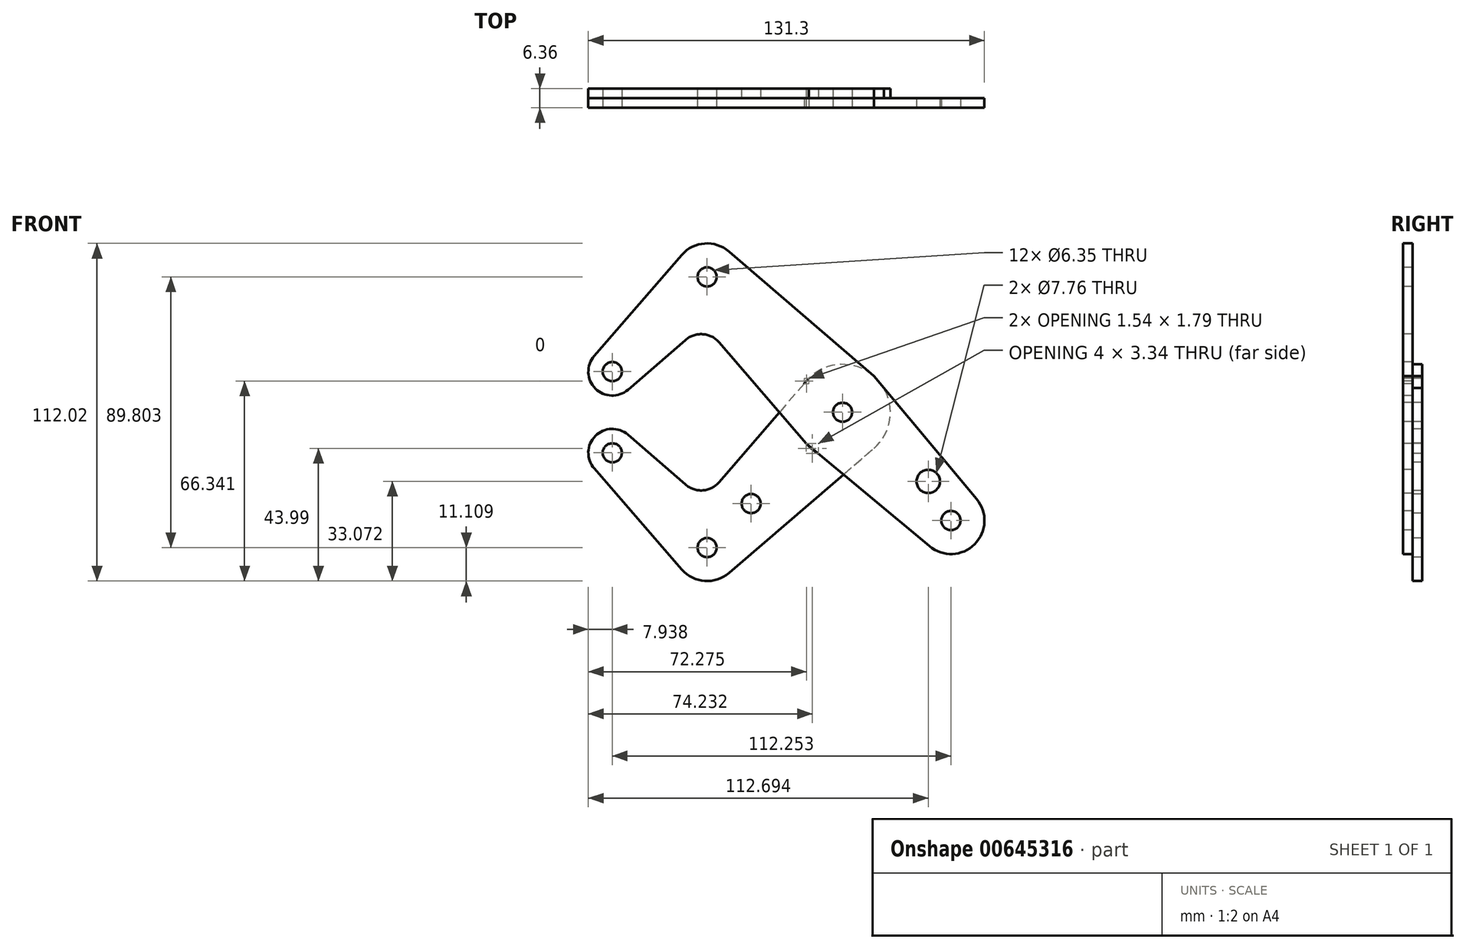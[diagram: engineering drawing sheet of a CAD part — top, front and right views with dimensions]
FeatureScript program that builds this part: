
annotation { "Feature Type Name" : "Feature", "Feature Type Description" : "" }
export const myFeature = defineFeature(function(context is Context, id is Id, definition is map)
    precondition{}
    {
        {
            var Q0;
            Q0=qCreatedBy(makeId("Front.planeOp"),FACE);
            var sketch = newSketch(context, id + "F0", { "sketchPlane" : qUnion([Q0])});
            skLineSegment(sketch, "E0", {"start": v(-76.33, 13.47) * mm, "end": v(-44.9, 44.9) * mm, "construction": true});
            skLineSegment(sketch, "E1", {"start": v(-44.9, 44.9) * mm, "end": v(35.92, -35.92) * mm, "construction": true});
            skCircle(sketch, "E2", {"center": v(-76.33, 13.47) * mm, "radius": 7.94 * mm});
            skCircle(sketch, "E3", {"center": v(-76.33, 13.47) * mm, "radius": 3.18 * mm});
            skCircle(sketch, "E4", {"center": v(-44.9, 44.9) * mm, "radius": 11.11 * mm});
            skCircle(sketch, "E5", {"center": v(-44.9, 44.9) * mm, "radius": 3.18 * mm});
            skCircle(sketch, "E6", {"center": v(0, 0) * mm, "radius": 15.88 * mm});
            skCircle(sketch, "E7", {"center": v(0, 0) * mm, "radius": 3.18 * mm});
            skCircle(sketch, "E8", {"center": v(35.92, -35.92) * mm, "radius": 3.18 * mm});
            skCircle(sketch, "E9", {"center": v(35.92, -35.92) * mm, "radius": 11.11 * mm});
            skCircle(sketch, "E10", {"center": v(0, 0) * mm, "radius": 3.98 * mm});
            skCircle(sketch, "E11", {"center": v(28.42, -22.94) * mm, "radius": 3.88 * mm});
            skLineSegment(sketch, "E12", {"start": v(-82.33, 18.67) * mm, "end": v(-53.3, 52.18) * mm});
            skLineSegment(sketch, "E13", {"start": v(-52.08, 23.98) * mm, "end": v(-71.13, 7.47) * mm});
            skLineSegment(sketch, "E14", {"start": v(-37.66, 53.33) * mm, "end": v(10.35, 12.04) * mm});
            skLineSegment(sketch, "E15", {"start": v(-40.85, 23.15) * mm, "end": v(-12.04, -10.35) * mm});
            skLineSegment(sketch, "E16", {"start": v(10.35, 12.04) * mm, "end": v(44.45, -28.8) * mm});
            skLineSegment(sketch, "E17", {"start": v(-12.04, -10.35) * mm, "end": v(28.8, -44.45) * mm});
            skArc(sketch, "E18.filletArc", {"start": v(-40.85, 23.15) * mm, "mid": v(-46.3, 25.9) * mm, "end": v(-52.08, 23.98) * mm});
            skLineSegment(sketch, "E19", {"start": v(0, 0) * mm, "end": v(-44.9, -44.9) * mm, "construction": true});
            skLineSegment(sketch, "E20", {"start": v(-44.9, -44.9) * mm, "end": v(-76.33, -13.47) * mm, "construction": true});
            skCircle(sketch, "E21", {"center": v(-76.33, -13.47) * mm, "radius": 3.18 * mm});
            skCircle(sketch, "E22", {"center": v(-76.33, -13.47) * mm, "radius": 7.94 * mm});
            skCircle(sketch, "E23", {"center": v(-44.9, -44.9) * mm, "radius": 3.18 * mm});
            skCircle(sketch, "E24", {"center": v(-44.9, -44.9) * mm, "radius": 11.11 * mm});
            skCircle(sketch, "E25", {"center": v(-30.3, -30.3) * mm, "radius": 3.18 * mm});
            skLineSegment(sketch, "E26", {"start": v(-82.33, -18.67) * mm, "end": v(-53.3, -52.18) * mm});
            skLineSegment(sketch, "E27", {"start": v(-71.13, -7.47) * mm, "end": v(-52.07, -23.98) * mm});
            skLineSegment(sketch, "E28", {"start": v(-37.66, -53.33) * mm, "end": v(10.35, -12.04) * mm});
            skLineSegment(sketch, "E29", {"start": v(-11.23, 11.23) * mm, "end": v(-40.84, -23.16) * mm});
            skPoint(sketch, "E30", {"position": v(-46.05, -29.2) * mm});
            skArc(sketch, "E31.filletArc", {"start": v(-52.07, -23.98) * mm, "mid": v(-46.29, -25.9) * mm, "end": v(-40.84, -23.16) * mm});
            skSolve(sketch);
        }
        {
            var Q0;
            {var subQ6=sQuery(id+"F0.wireOp",EDGE,"E12");Q0=makeQuery(id+"F0.imprint","IMPRINT",FACE,{"disambiguationData":[TD([[makeQuery(id+"F0.imprint","IMPRINT",EDGE,{"derivedFrom":subQ6}),-1.0]])]});}
            var Q1;
            Q1=makeQuery(id+"F0.imprint","IMPRINT",FACE,{"disambiguationData":[TD([[makeQuery(id+"F0.imprint","IMPRINT",EDGE,{"derivedFrom":sQuery(id+"F0.wireOp",EDGE,"E3")}),-1.0]])]});
            var Q2;
            Q2=makeQuery(id+"F0.imprint","IMPRINT",FACE,{"disambiguationData":[TD([[makeQuery(id+"F0.imprint","IMPRINT",EDGE,{"derivedFrom":sQuery(id+"F0.wireOp",EDGE,"E5")}),-1.0]])]});
            var Q3;
            Q3=makeQuery(id+"F0.imprint","IMPRINT",FACE,{"disambiguationData":[TD([[makeQuery(id+"F0.imprint","IMPRINT",EDGE,{"derivedFrom":sQuery(id+"F0.wireOp",EDGE,"E10")}),-1.0]])]});
            var Q4;
            Q4=makeQuery(id+"F0.imprint","IMPRINT",FACE,{"disambiguationData":[TD([[makeQuery(id+"F0.imprint","IMPRINT",EDGE,{"derivedFrom":sQuery(id+"F0.wireOp",EDGE,"E7")}),-1.0]])]});
            var Q5;
            {var subQ0=sQuery(id+"F0.wireOp",EDGE,"E15");var subQ3=sQuery(id+"F0.wireOp",EDGE,"E29");var subQ5=makeQuery(id+"F0.imprint","INTERSECT",VERTEX,{"derivedFrom":[subQ0,subQ3]});Q5=makeQuery(id+"F0.imprint","IMPRINT",FACE,{"disambiguationData":[TD([[makeQuery(id+"F0.imprint","IMPRINT",EDGE,{"disambiguationData":[TD([[subQ5,1.0]])],"derivedFrom":subQ3}),1.0]])]});}
            var Q6;
            {var subQ0=sQuery(id+"F0.wireOp",EDGE,"E28");var subQ1=sQuery(id+"F0.wireOp",EDGE,"E6");var subQ2=makeQuery(id+"F0.imprint","INTERSECT",VERTEX,{"derivedFrom":[subQ1,subQ0]});Q6=makeQuery(id+"F0.imprint","IMPRINT",FACE,{"disambiguationData":[TD([[makeQuery(id+"F0.imprint","IMPRINT",EDGE,{"disambiguationData":[TD([[subQ2,1.0]])],"derivedFrom":subQ1}),-1.0]])]});}
            var Q7;
            {var subQ0=sQuery(id+"F0.wireOp",EDGE,"E11");Q7=makeQuery(id+"F0.imprint","IMPRINT",FACE,{"disambiguationData":[TD([[makeQuery(id+"F0.imprint","IMPRINT",EDGE,{"derivedFrom":subQ0}),-1.0]])]});}
            var Q8;
            Q8=makeQuery(id+"F0.imprint","IMPRINT",FACE,{"disambiguationData":[TD([[makeQuery(id+"F0.imprint","IMPRINT",EDGE,{"derivedFrom":sQuery(id+"F0.wireOp",EDGE,"E8")}),-1.0]])]});
            extrude(context, id + "F1", {"entities" : qUnion([Q0, Q1, Q2, Q3, Q4, Q5, Q6, Q7, Q8]), "depth" : 3.17 * mm, "offsetDistance" : 25.4 * mm});
        }
        {
            var Q0;
            Q0=makeQuery(id+"F0.imprint","IMPRINT",FACE,{"disambiguationData":[TD([[makeQuery(id+"F0.imprint","IMPRINT",EDGE,{"derivedFrom":sQuery(id+"F0.wireOp",EDGE,"E21")}),-1.0]])]});
            var Q1;
            Q1=makeQuery(id+"F0.imprint","IMPRINT",FACE,{"disambiguationData":[TD([[makeQuery(id+"F0.imprint","IMPRINT",EDGE,{"derivedFrom":sQuery(id+"F0.wireOp",EDGE,"E25")}),-1.0]])]});
            var Q2;
            Q2=makeQuery(id+"F0.imprint","IMPRINT",FACE,{"disambiguationData":[TD([[makeQuery(id+"F0.imprint","IMPRINT",EDGE,{"derivedFrom":sQuery(id+"F0.wireOp",EDGE,"E23")}),-1.0]])]});
            var Q3;
            Q3=makeQuery(id+"F1.opExtrude","CAP_FACE",FACE,{"disambiguationData":[OSD([sQuery(id+"F0.wireOp",EDGE,"E2"),sQuery(id+"F0.wireOp",EDGE,"E3"),sQuery(id+"F0.wireOp",EDGE,"E4"),sQuery(id+"F0.wireOp",EDGE,"E5"),sQuery(id+"F0.wireOp",EDGE,"E6"),sQuery(id+"F0.wireOp",EDGE,"E7"),sQuery(id+"F0.wireOp",EDGE,"E8"),sQuery(id+"F0.wireOp",EDGE,"E9"),sQuery(id+"F0.wireOp",EDGE,"E11"),sQuery(id+"F0.wireOp",EDGE,"E12"),sQuery(id+"F0.wireOp",EDGE,"E13"),sQuery(id+"F0.wireOp",EDGE,"E14"),sQuery(id+"F0.wireOp",EDGE,"E15"),sQuery(id+"F0.wireOp",EDGE,"E16"),sQuery(id+"F0.wireOp",EDGE,"E17"),sQuery(id+"F0.wireOp",EDGE,"E18.filletArc"),sQuery(id+"F0.wireOp",EDGE,"E29")])],"isStart":false});
            var Q4;
            {var subQ0=sQuery(id+"F0.wireOp",EDGE,"E15");var subQ3=sQuery(id+"F0.wireOp",EDGE,"E29");var subQ5=makeQuery(id+"F0.imprint","INTERSECT",VERTEX,{"derivedFrom":[subQ0,subQ3]});Q4=makeQuery(id+"F0.imprint","IMPRINT",FACE,{"disambiguationData":[TD([[makeQuery(id+"F0.imprint","IMPRINT",EDGE,{"disambiguationData":[TD([[subQ5,1.0]])],"derivedFrom":subQ3}),1.0]])]});}
            var Q5;
            Q5=makeQuery(id+"F0.imprint","IMPRINT",FACE,{"disambiguationData":[TD([[makeQuery(id+"F0.imprint","IMPRINT",EDGE,{"derivedFrom":sQuery(id+"F0.wireOp",EDGE,"E10")}),-1.0]])]});
            var Q6;
            {var subQ0=sQuery(id+"F0.wireOp",EDGE,"E28");var subQ1=sQuery(id+"F0.wireOp",EDGE,"E6");var subQ2=makeQuery(id+"F0.imprint","INTERSECT",VERTEX,{"derivedFrom":[subQ1,subQ0]});Q6=makeQuery(id+"F0.imprint","IMPRINT",FACE,{"disambiguationData":[TD([[makeQuery(id+"F0.imprint","IMPRINT",EDGE,{"disambiguationData":[TD([[subQ2,1.0]])],"derivedFrom":subQ1}),-1.0]])]});}
            var Q7;
            Q7=makeQuery(id+"F0.imprint","IMPRINT",FACE,{"disambiguationData":[TD([[makeQuery(id+"F0.imprint","IMPRINT",EDGE,{"derivedFrom":sQuery(id+"F0.wireOp",EDGE,"E7")}),-1.0]])]});
            extrude(context, id + "F2", {"entities" : qUnion([Q0, Q1, Q2, Q3, Q4, Q5, Q6, Q7]), "oppositeDirection" : true, "depth" : 3.17 * mm, "offsetDistance" : 25.4 * mm});
        }
    });
